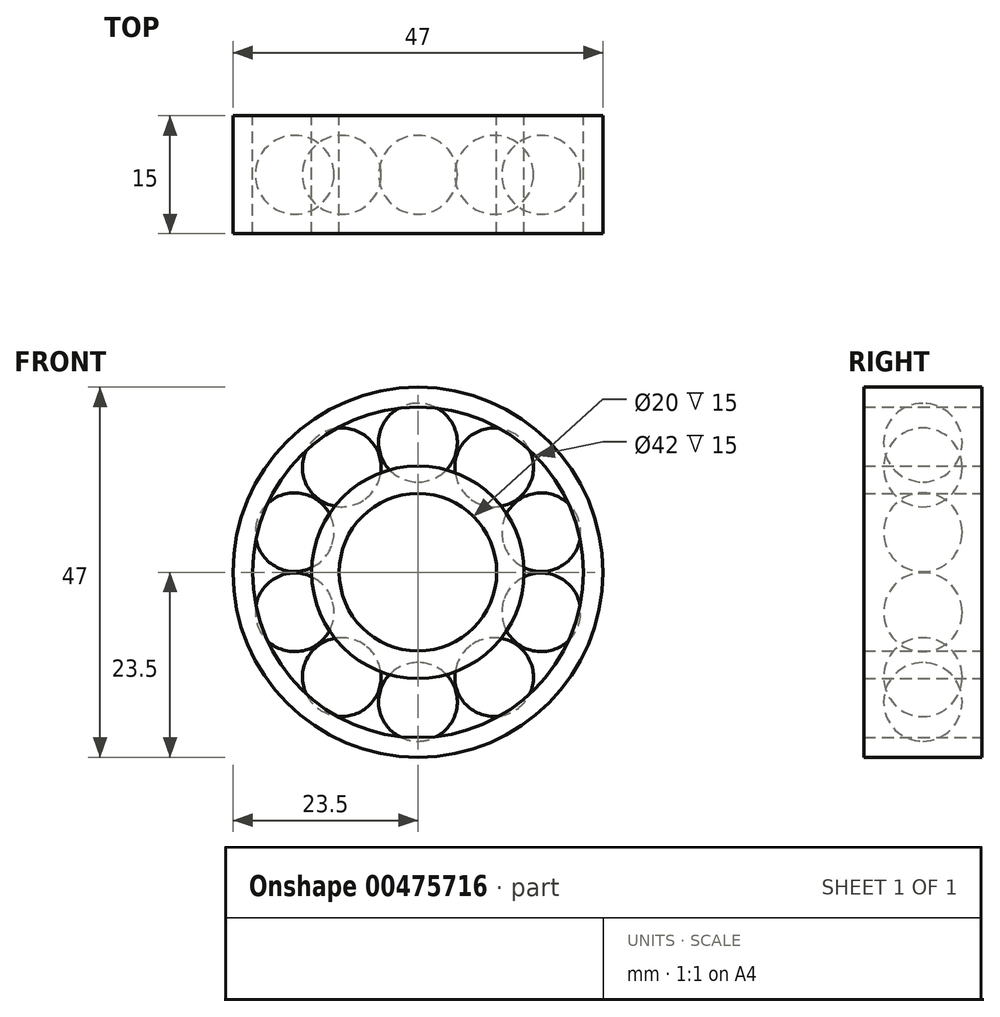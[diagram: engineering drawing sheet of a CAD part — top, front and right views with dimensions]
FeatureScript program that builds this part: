
annotation { "Feature Type Name" : "Feature", "Feature Type Description" : "" }
export const myFeature = defineFeature(function(context is Context, id is Id, definition is map)
    precondition{}
    {
        {
            var Q0;
            Q0=qCreatedBy(makeId("Front.planeOp"),FACE);
            var sketch = newSketch(context, id + "F0", { "sketchPlane" : qUnion([Q0])});
            skCircle(sketch, "E0", {"center": v(0, 0) * mm, "radius": 21 * mm});
            skCircle(sketch, "E1", {"center": v(0, 0) * mm, "radius": 10 * mm});
            skCircle(sketch, "E2", {"center": v(0, 0) * mm, "radius": 13.5 * mm});
            skCircle(sketch, "E3", {"center": v(0, 0) * mm, "radius": 23.5 * mm});
            skSolve(sketch);
        }
        {
            var Q0;
            Q0=makeQuery(id+"F0.imprint","IMPRINT",FACE,{"disambiguationData":[TD([[makeQuery(id+"F0.imprint","IMPRINT",EDGE,{"derivedFrom":sQuery(id+"F0.wireOp",EDGE,"E0")}),-1.0]])]});
            extrude(context, id + "F1", {"entities" : qUnion([Q0]), "depth" : 15 * mm});
        }
        {
            var Q0;
            Q0=makeQuery(id+"F0.imprint","IMPRINT",FACE,{"disambiguationData":[TD([[makeQuery(id+"F0.imprint","IMPRINT",EDGE,{"derivedFrom":sQuery(id+"F0.wireOp",EDGE,"E1")}),-1.0]])]});
            extrude(context, id + "F2", {"entities" : qUnion([Q0]), "depth" : 15 * mm});
        }
        {
            var Q0;
            Q0=qCreatedBy(makeId("Front.planeOp"),FACE);
            cPlane(context, id + "F3", {"entities" : qUnion([Q0]), "cplaneType" : CPlaneType.OFFSET, "offset" : 7.5 * mm, "width" : 150 * mm, "height" : 150 * mm});
        }
        {
            var Q0;
            Q0=qCreatedBy(id+"F3.planeOp",FACE);
            var sketch = newSketch(context, id + "F4", { "sketchPlane" : qUnion([Q0])});
            skArc(sketch, "E4", {"start": v(0, 11.46) * mm, "mid": v(5, 16.46) * mm, "end": v(0, 21.46) * mm});
            skLineSegment(sketch, "E5", {"start": v(0, 21.46) * mm, "end": v(0, 11.46) * mm});
            skSolve(sketch);
        }
        {
            var Q0;
            Q0=makeQuery(id+"F4.imprint","IMPRINT",FACE,{"disambiguationData":[TD([[makeQuery(id+"F4.imprint","IMPRINT",EDGE,{"derivedFrom":sQuery(id+"F4.wireOp",EDGE,"E4")}),1.0]])]});
            var Q1;
            Q1=sQuery(id+"F4.wireOp",EDGE,"E5");
            revolve(context, id + "F5", {"entities" : qUnion([Q0]), "axis" : qUnion([Q1]), "revolveType" : RevolveType.FULL});
        }
        {
            var Q0;
            Q0=makeQuery(id+"F5.opRevolve","SWEPT_BODY",BODY,{"disambiguationData":[OSD([sQuery(id+"F4.wireOp",EDGE,"E4"),sQuery(id+"F4.wireOp",EDGE,"E5")])]});
            var Q1;
            Q1=makeQuery(id+"F2.opExtrude","CAP_EDGE",EDGE,{"disambiguationData":[OSD([sQuery(id+"F0.wireOp",EDGE,"E2")])],"isStart":false});
            circularPattern(context, id + "F6", {"entities" : qUnion([Q0]), "axis" : qUnion([Q1]), "angle" : 360 * degree, "instanceCount" : 10, "equalSpace" : true});
        }
    });
